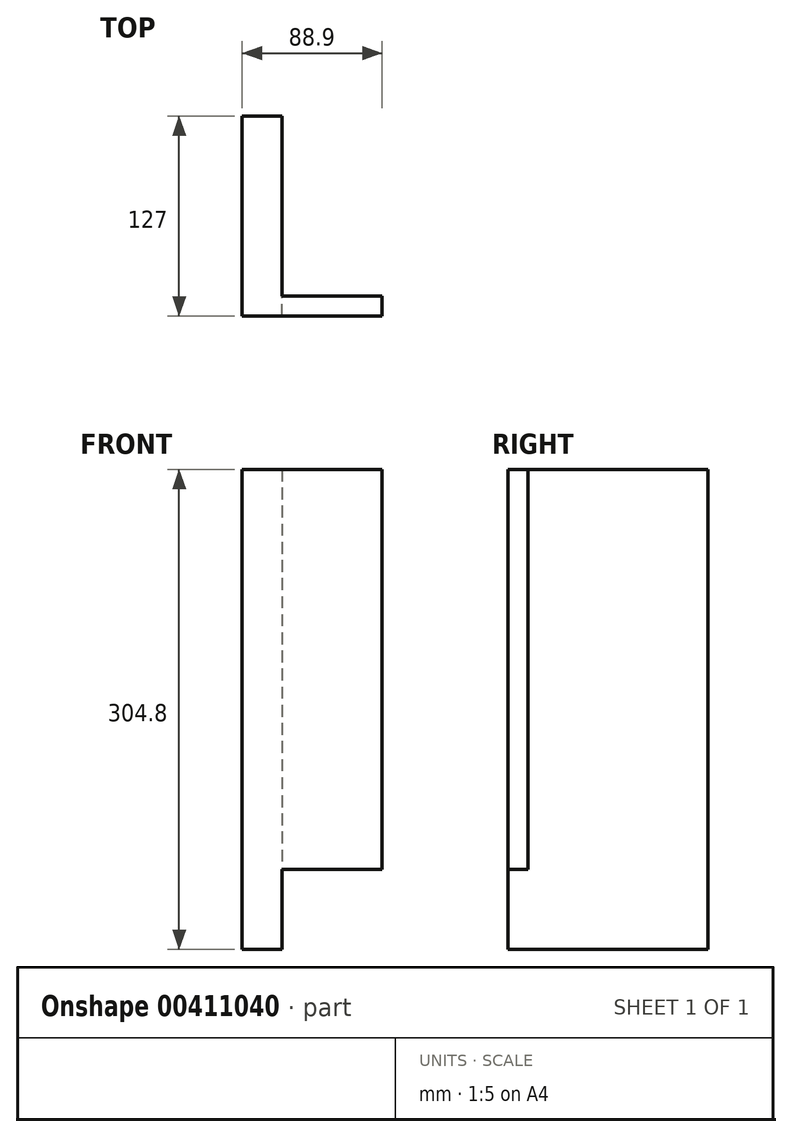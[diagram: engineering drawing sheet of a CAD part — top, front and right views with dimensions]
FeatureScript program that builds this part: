
annotation { "Feature Type Name" : "Feature", "Feature Type Description" : "" }
export const myFeature = defineFeature(function(context is Context, id is Id, definition is map)
    precondition{}
    {
        {
            var Q0;
            Q0=qCreatedBy(makeId("Top.planeOp"),FACE);
            var sketch = newSketch(context, id + "F0", { "sketchPlane" : qUnion([Q0])});
            skLineSegment(sketch, "E0.bottom", {"start": v(0, 0) * mm, "end": v(25.4, 0) * mm});
            skLineSegment(sketch, "E0.top", {"start": v(0, 127) * mm, "end": v(25.4, 127) * mm});
            skLineSegment(sketch, "E0.left", {"start": v(0, 0) * mm, "end": v(0, 127) * mm});
            skLineSegment(sketch, "E0.right", {"start": v(25.4, 0) * mm, "end": v(25.4, 127) * mm});
            skLineSegment(sketch, "E1.bottom", {"start": v(25.4, 0) * mm, "end": v(88.9, 0) * mm});
            skLineSegment(sketch, "E1.top", {"start": v(25.4, 12.7) * mm, "end": v(88.9, 12.7) * mm});
            skLineSegment(sketch, "E1.left", {"start": v(25.4, 0) * mm, "end": v(25.4, 12.7) * mm});
            skLineSegment(sketch, "E1.right", {"start": v(88.9, 0) * mm, "end": v(88.9, 12.7) * mm});
            skSolve(sketch);
        }
        {
            var Q0;
            Q0=makeQuery(id+"F0.imprint","IMPRINT",FACE,{"disambiguationData":[TD([[makeQuery(id+"F0.imprint","IMPRINT",EDGE,{"derivedFrom":sQuery(id+"F0.wireOp",EDGE,"E0.bottom")}),1.0]])]});
            extrude(context, id + "F1", {"entities" : qUnion([Q0]), "depth" : 304.8 * mm});
        }
        {
            var Q0;
            Q0=makeQuery(id+"F0.imprint","IMPRINT",FACE,{"disambiguationData":[TD([[makeQuery(id+"F0.imprint","IMPRINT",EDGE,{"derivedFrom":sQuery(id+"F0.wireOp",EDGE,"E1.bottom")}),1.0]])]});
            var Q1;
            Q1=makeQuery(id+"F1.opExtrude","CAP_FACE",FACE,{"disambiguationData":[OSD([sQuery(id+"F0.wireOp",EDGE,"E0.bottom"),sQuery(id+"F0.wireOp",EDGE,"E0.top"),sQuery(id+"F0.wireOp",EDGE,"E0.left"),sQuery(id+"F0.wireOp",EDGE,"E0.right"),sQuery(id+"F0.wireOp",EDGE,"E1.left")])],"isStart":false});
            extrude(context, id + "F2", {"entities" : qUnion([Q0]), "operationType" : NewBodyOperationType.ADD, "endBound" : BoundingType.UP_TO_SURFACE, "endBoundEntityFace" : qUnion([Q1]), "depth" : 25.4 * mm, "hasSecondDirection" : true, "secondDirectionOppositeDirection" : false, "secondDirectionDepth" : 50.8 * mm});
        }
    });
